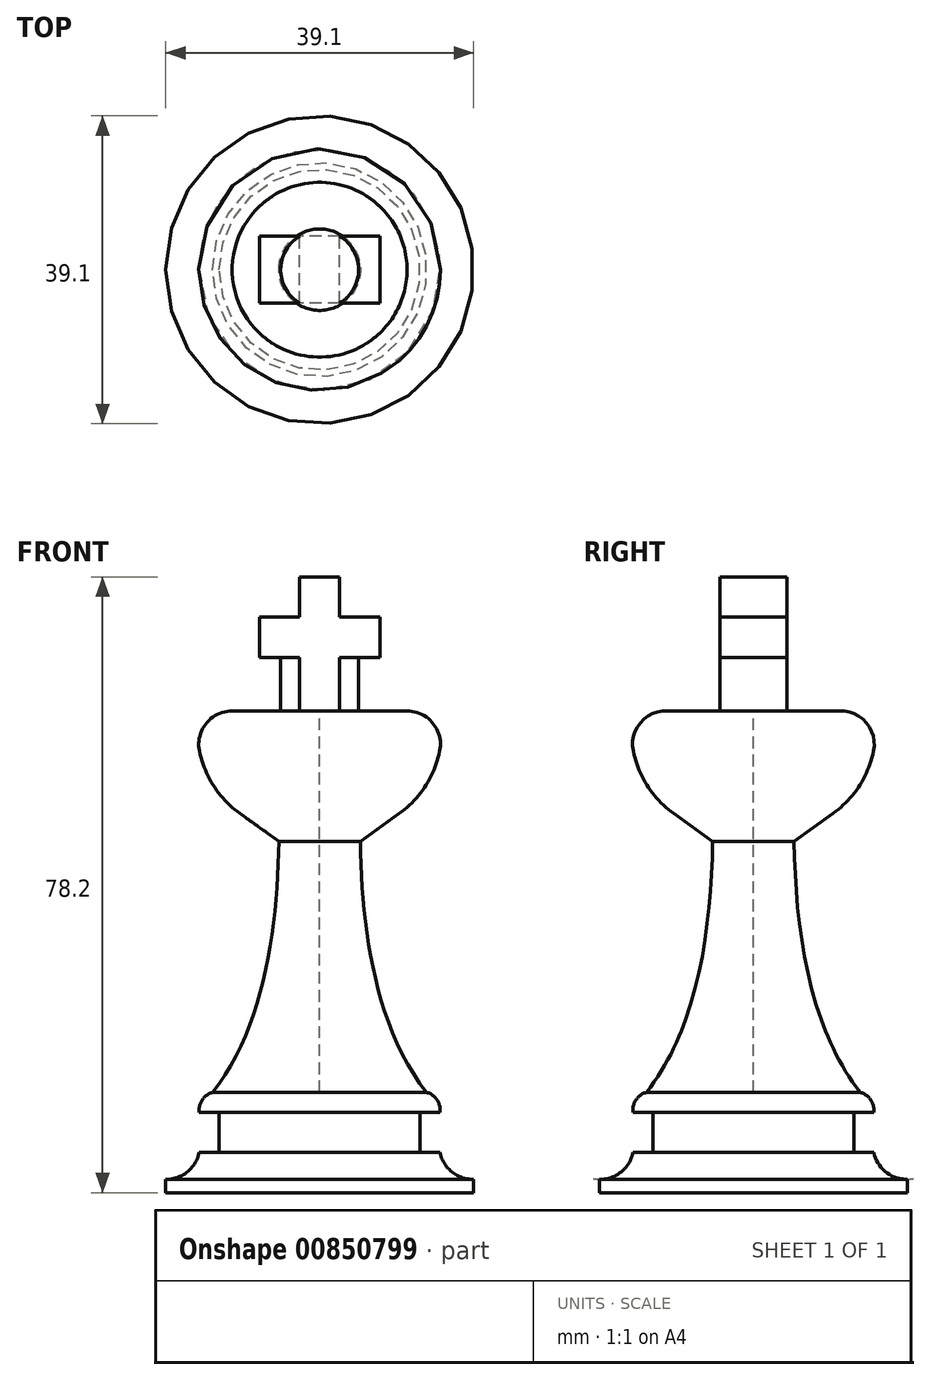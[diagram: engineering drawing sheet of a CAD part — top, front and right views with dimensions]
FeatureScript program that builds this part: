
annotation { "Feature Type Name" : "Feature", "Feature Type Description" : "" }
export const myFeature = defineFeature(function(context is Context, id is Id, definition is map)
    precondition{}
    {
        {
            var Q0;
            Q0=qCreatedBy(makeId("Front.planeOp"),FACE);
            var sketch = newSketch(context, id + "F0", { "sketchPlane" : qUnion([Q0])});
            skLineSegment(sketch, "E0", {"start": v(0, 0) * mm, "end": v(11.5, 0) * mm});
            skLineSegment(sketch, "E1", {"start": v(11.5, 0) * mm, "end": v(11.5, 1) * mm});
            skLineSegment(sketch, "E2", {"start": v(9, 3) * mm, "end": v(7.5, 3) * mm});
            skLineSegment(sketch, "E3", {"start": v(7.5, 3) * mm, "end": v(7.5, 6) * mm});
            skLineSegment(sketch, "E4", {"start": v(7.5, 6) * mm, "end": v(9, 6) * mm});
            skPoint(sketch, "E5", {"position": v(10.25, 1.06) * mm});
            skPoint(sketch, "E6", {"position": v(9, 2.06) * mm});
            skPoint(sketch, "E7", {"position": v(9.03, 6.8) * mm});
            skLineSegment(sketch, "E8", {"start": v(8, 7.5) * mm, "end": v(0, 7.5) * mm});
            skPoint(sketch, "E9.trimOffspring.end.orphan", {"position": v(9.06, 7.62) * mm});
            skPoint(sketch, "E10.orphan", {"position": v(9, 1.12) * mm});
            skLineSegment(sketch, "E11", {"start": v(0, 0) * mm, "end": v(0, 7.5) * mm});
            skLineSegment(sketch, "E12", {"start": v(0, 0) * mm, "end": v(0, 0) * mm});
            skLineSegment(sketch, "E13", {"start": v(0, 36) * mm, "end": v(0, 7.5) * mm});
            skLineSegment(sketch, "E14", {"start": v(0, 0) * mm, "end": v(0, 46) * mm});
            skLineSegment(sketch, "E15", {"start": v(0, 46) * mm, "end": v(11.5, 46) * mm});
            skLineSegment(sketch, "E16.MirrorCS", {"start": v(0, 46) * mm, "end": v(-11.5, 46) * mm});
            skLineSegment(sketch, "E17.MirrorCS", {"start": v(-8, 36) * mm, "end": v(0, 36) * mm});
            skPoint(sketch, "E18", {"position": v(0, 36) * mm});
            skFitSpline(sketch, "E19", {"points": [v(8, 7.5) * mm, v(3.04, 26.25) * mm], "startDerivative": vector(-11.5, 14.24) * mm, "endDerivative": vector(-0.28, 19.4) * mm});
            skArc(sketch, "E20", {"start": v(9, 3) * mm, "mid": v(9.89, 1.55) * mm, "end": v(11.5, 1) * mm});
            skArc(sketch, "E21", {"start": v(9, 6) * mm, "mid": v(8.77, 6.93) * mm, "end": v(8, 7.5) * mm});
            skLineSegment(sketch, "E22", {"start": v(3.04, 26.25) * mm, "end": v(5.95, 28.34) * mm});
            skLineSegment(sketch, "E23", {"start": v(0, 36) * mm, "end": v(9, 36) * mm});
            skArc(sketch, "E24", {"start": v(5.95, 28.34) * mm, "mid": v(8.6, 31.72) * mm, "end": v(9, 36) * mm});
            skSolve(sketch);
        }
        {
            var Q0;
            Q0=makeQuery(id+"F0.imprint","IMPRINT",FACE,{"disambiguationData":[TD([[makeQuery(id+"F0.imprint","IMPRINT",EDGE,{"derivedFrom":sQuery(id+"F0.wireOp",EDGE,"E8")}),-1.0]])]});
            var Q1;
            Q1=makeQuery(id+"F0.imprint","IMPRINT",FACE,{"disambiguationData":[TD([[makeQuery(id+"F0.imprint","IMPRINT",EDGE,{"derivedFrom":sQuery(id+"F0.wireOp",EDGE,"E1")}),1.0]])]});
            var Q2;
            Q2=makeQuery(id+"F0.imprint","IMPRINT",FACE,{"disambiguationData":[TD([[makeQuery(id+"F0.imprint","IMPRINT",EDGE,{"derivedFrom":sQuery(id+"F0.wireOp",EDGE,"JUtDv52K-AW70-VZSI-xevH-zfGwWtPnm6Iz")}),-1.0]])]});
            var Q3;
            Q3=sQuery(id+"F0.wireOp",EDGE,"E11");
            revolve(context, id + "F1", {"entities" : qUnion([Q0, Q1, Q2]), "axis" : qUnion([Q3]), "revolveType" : RevolveType.FULL});
        }
        {
            var Q0;
            Q0=qCreatedBy(makeId("Front.planeOp"),FACE);
            var sketch = newSketch(context, id + "F2", { "sketchPlane" : qUnion([Q0])});
            skLineSegment(sketch, "E25", {"start": v(0, 0) * mm, "end": v(0, 36) * mm});
            skLineSegment(sketch, "E26", {"start": v(0, 36) * mm, "end": v(2.92, 36) * mm});
            skLineSegment(sketch, "E27", {"start": v(1.5, 40) * mm, "end": v(4.5, 40) * mm});
            skLineSegment(sketch, "E28", {"start": v(4.5, 40) * mm, "end": v(4.5, 43) * mm});
            skLineSegment(sketch, "E29", {"start": v(4.5, 43) * mm, "end": v(1.5, 43) * mm});
            skLineSegment(sketch, "E30", {"start": v(1.5, 43) * mm, "end": v(1.5, 46) * mm});
            skLineSegment(sketch, "E31", {"start": v(1.5, 46) * mm, "end": v(0, 46) * mm});
            skLineSegment(sketch, "E32", {"start": v(0, 46) * mm, "end": v(0, 36) * mm});
            skLineSegment(sketch, "E33.MirrorCS", {"start": v(-1.5, 40) * mm, "end": v(-4.5, 40) * mm});
            skLineSegment(sketch, "E34.MirrorCS", {"start": v(0, 36) * mm, "end": v(-1.5, 36) * mm});
            skLineSegment(sketch, "E35.MirrorCS", {"start": v(-4.5, 40) * mm, "end": v(-4.5, 43) * mm});
            skLineSegment(sketch, "E36.MirrorCS", {"start": v(-4.5, 43) * mm, "end": v(-1.5, 43) * mm});
            skLineSegment(sketch, "E37.MirrorCS", {"start": v(-1.5, 43) * mm, "end": v(-1.5, 46) * mm});
            skLineSegment(sketch, "E38.MirrorCS", {"start": v(-1.5, 46) * mm, "end": v(0, 46) * mm});
            skLineSegment(sketch, "E39", {"start": v(-1.5, 40) * mm, "end": v(1.5, 40) * mm});
            skLineSegment(sketch, "E40", {"start": v(2.92, 36) * mm, "end": v(2.92, 40) * mm});
            skPoint(sketch, "E40.endSnap0", {"position": v(3, 40) * mm});
            skSolve(sketch);
        }
        {
            var Q0;
            {var subQ1=sQuery(id+"F2.wireOp",EDGE,"E26");Q0=makeQuery(id+"F2.imprint","IMPRINT",FACE,{"disambiguationData":[TD([[makeQuery(id+"F2.imprint","IMPRINT",EDGE,{"derivedFrom":subQ1}),1.0]])]});}
            var Q1;
            Q1=sQuery(id+"F2.wireOp",EDGE,"E32");
            revolve(context, id + "F3", {"operationType" : NewBodyOperationType.ADD, "entities" : qUnion([Q0]), "axis" : qUnion([Q1]), "revolveType" : RevolveType.FULL});
        }
        {
            var Q0;
            {var subQ0=sQuery(id+"F2.wireOp",EDGE,"E27");Q0=makeQuery(id+"F2.imprint","IMPRINT",FACE,{"disambiguationData":[TD([[makeQuery(id+"F2.imprint","IMPRINT",EDGE,{"derivedFrom":subQ0}),1.0]])]});}
            var Q1;
            {var subQ0=sQuery(id+"F2.wireOp",EDGE,"E33.MirrorCS");Q1=makeQuery(id+"F2.imprint","IMPRINT",FACE,{"disambiguationData":[TD([[makeQuery(id+"F2.imprint","IMPRINT",EDGE,{"derivedFrom":subQ0}),-1.0]])]});}
            extrude(context, id + "F4", {"entities" : qUnion([Q0, Q1]), "operationType" : NewBodyOperationType.ADD, "endBound" : BoundingType.SYMMETRIC, "depth" : 5 * mm, "offsetDistance" : 25 * mm});
        }
        {
            var Q0;
            Q0=makeQuery(id+"F1.opRevolve","SWEPT_EDGE",EDGE,{"disambiguationData":[OSD([sQuery(id+"F0.wireOp",EDGE,"E23"),sQuery(id+"F0.wireOp",EDGE,"E24")])]});
            fillet(context, id + "F5", {"entities" : qUnion([Q0]), "radius" : 2.5 * mm, "tangentPropagation" : true, "allowEdgeOverflow" : false});
        }
        {
            var Q0;
            Q0=qCreatedBy(makeId("Front.planeOp"),FACE);
            cPlane(context, id + "F6", {"entities" : qUnion([Q0]), "cplaneType" : CPlaneType.OFFSET, "offset" : 2.5 * mm, "oppositeDirection" : true, "width" : 150 * mm, "height" : 150 * mm});
        }
        {
            var Q0;
            Q0=qCreatedBy(makeId("Front.planeOp"),FACE);
            cPlane(context, id + "F7", {"entities" : qUnion([Q0]), "cplaneType" : CPlaneType.OFFSET, "offset" : 2.5 * mm, "width" : 150 * mm, "height" : 150 * mm});
        }
        {
            var Q0;
            Q0=qCreatedBy(id+"F6.planeOp",FACE);
            var sketch = newSketch(context, id + "F8", { "sketchPlane" : qUnion([Q0])});
            skPoint(sketch, "E41.0", {"position": v(-4.5, 40) * mm});
            skPoint(sketch, "E42.0", {"position": v(4.5, 40) * mm});
            skPoint(sketch, "E43.0", {"position": v(4.5, 36) * mm});
            skLineSegment(sketch, "E44.0", {"start": v(-4.5, 40) * mm, "end": v(-4.5, 43) * mm});
            skLineSegment(sketch, "E45.bottom", {"start": v(-4.5, 40) * mm, "end": v(4.5, 40) * mm});
            skLineSegment(sketch, "E45.top", {"start": v(-4.5, 36) * mm, "end": v(4.5, 36) * mm});
            skLineSegment(sketch, "E45.left", {"start": v(-4.5, 40) * mm, "end": v(-4.5, 36) * mm});
            skLineSegment(sketch, "E45.right", {"start": v(4.5, 40) * mm, "end": v(4.5, 36) * mm});
            skSolve(sketch);
        }
        {
            var Q0;
            Q0=makeQuery(id+"F8.imprint","IMPRINT",FACE,{"disambiguationData":[TD([[makeQuery(id+"F8.imprint","IMPRINT",EDGE,{"derivedFrom":sQuery(id+"F8.wireOp",EDGE,"E45.bottom")}),-1.0]])]});
            extrude(context, id + "F9", {"entities" : qUnion([Q0]), "operationType" : NewBodyOperationType.REMOVE, "oppositeDirection" : true, "depth" : 3 * mm, "offsetDistance" : 25 * mm});
        }
        {
            var Q0;
            Q0=qCreatedBy(id+"F7.planeOp",FACE);
            var sketch = newSketch(context, id + "F10", { "sketchPlane" : qUnion([Q0])});
            skPoint(sketch, "E46.0", {"position": v(-4.5, 40) * mm});
            skPoint(sketch, "E47.0", {"position": v(4.5, 40) * mm});
            skPoint(sketch, "E48.0", {"position": v(4.5, 36) * mm});
            skLineSegment(sketch, "E49.bottom", {"start": v(-4.5, 40) * mm, "end": v(4.5, 40) * mm});
            skLineSegment(sketch, "E49.top", {"start": v(-4.5, 36) * mm, "end": v(4.5, 36) * mm});
            skLineSegment(sketch, "E49.left", {"start": v(-4.5, 40) * mm, "end": v(-4.5, 36) * mm});
            skLineSegment(sketch, "E49.right", {"start": v(4.5, 40) * mm, "end": v(4.5, 36) * mm});
            skSolve(sketch);
        }
        {
            var Q0;
            Q0=makeQuery(id+"F10.imprint","IMPRINT",FACE,{"disambiguationData":[TD([[makeQuery(id+"F10.imprint","IMPRINT",EDGE,{"derivedFrom":sQuery(id+"F10.wireOp",EDGE,"E49.bottom")}),-1.0]])]});
            extrude(context, id + "F11", {"entities" : qUnion([Q0]), "operationType" : NewBodyOperationType.REMOVE, "depth" : 3 * mm, "offsetDistance" : 25 * mm});
        }
        {
            var Q0;
            Q0=makeQuery(id+"F1.opRevolve","SWEPT_BODY",BODY,{"disambiguationData":[OSD([sQuery(id+"F0.wireOp",EDGE,"E1"),sQuery(id+"F0.wireOp",EDGE,"E2"),sQuery(id+"F0.wireOp",EDGE,"E3"),sQuery(id+"F0.wireOp",EDGE,"E4"),sQuery(id+"F0.wireOp",EDGE,"ed9daf73-08ae-4b3e-b13f-b86e1b38dbdd"),sQuery(id+"F0.wireOp",EDGE,"ffb9664f-d90a-4bed-93c2-dfbb747daa0b"),sQuery(id+"F0.wireOp",EDGE,"E0"),sQuery(id+"F0.wireOp",EDGE,"E13"),sQuery(id+"F0.wireOp",EDGE,"E14"),sQuery(id+"F0.wireOp",EDGE,"oe8KpcPt-ODok-d8mT-Kdy5-Pr5gFS03Bgs6"),sQuery(id+"F0.wireOp",EDGE,"E19"),sQuery(id+"F0.wireOp",EDGE,"yJasaVeY-0GzQ-78Dt-LxTq-eVvgsLxdQeU0"),sQuery(id+"F0.wireOp",EDGE,"lZ6j52ky-CSWV-olG8-BYVF-fcFUQGHKq88Z"),sQuery(id+"F0.wireOp",EDGE,"JUtDv52K-AW70-VZSI-xevH-zfGwWtPnm6Iz")])]});
            var Q1;
            Q1=qCreatedBy(makeId("Origin.pointOp"),VERTEX);
            transform(context, id + "F12", {"entities" : qUnion([Q0]), "transformType" : TransformType.SCALE_UNIFORMLY, "scale" : 1.7, "scalePoint" : qUnion([Q1]), "makeCopy" : false});
        }
    });
